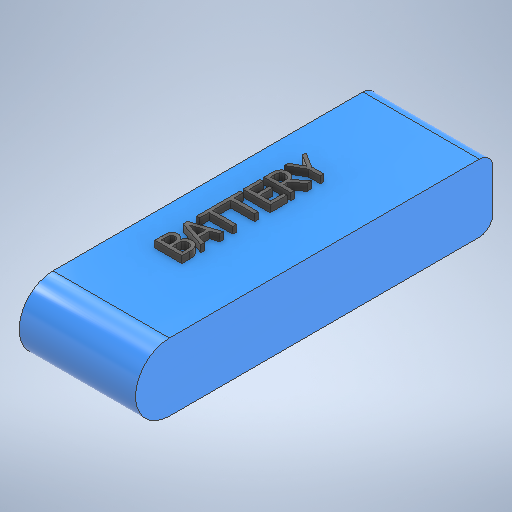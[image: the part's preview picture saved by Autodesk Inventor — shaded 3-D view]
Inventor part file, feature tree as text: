
AUTODESK INVENTOR PART (.ipt)
format: ipt  version: 2025.2 (Build 292293000, 293)  size: 371,200 bytes
history: native  units: mm
features: extrude x2, fillet x2, sketch x2
ambient origin geometry x8: Origin, YZ Plane, XZ Plane, XY Plane, X Axis, Y Axis, Z Axis, Center Point
bodies: Solid1 (feature_tree)
feature tree (6):
  extrude  "Extrusion1"  Depth=132.0mm
  fillet  "Fillet1"  Radius=25.0mm
  fillet  "Fillet2"  Radius=12.5mm
  extrude  "Extrusion2"  Depth=2.5mm TaperAngle=0.0deg
  sketch  "Sketch1"  dims[d0=43.0mm d1=132.0mm d2=25.0mm d3=0.0mm d4=12.5mm]
  sketch  "Sketch2"  dims[d5=5.0mm d6=2.5mm d7=0.0mm]
